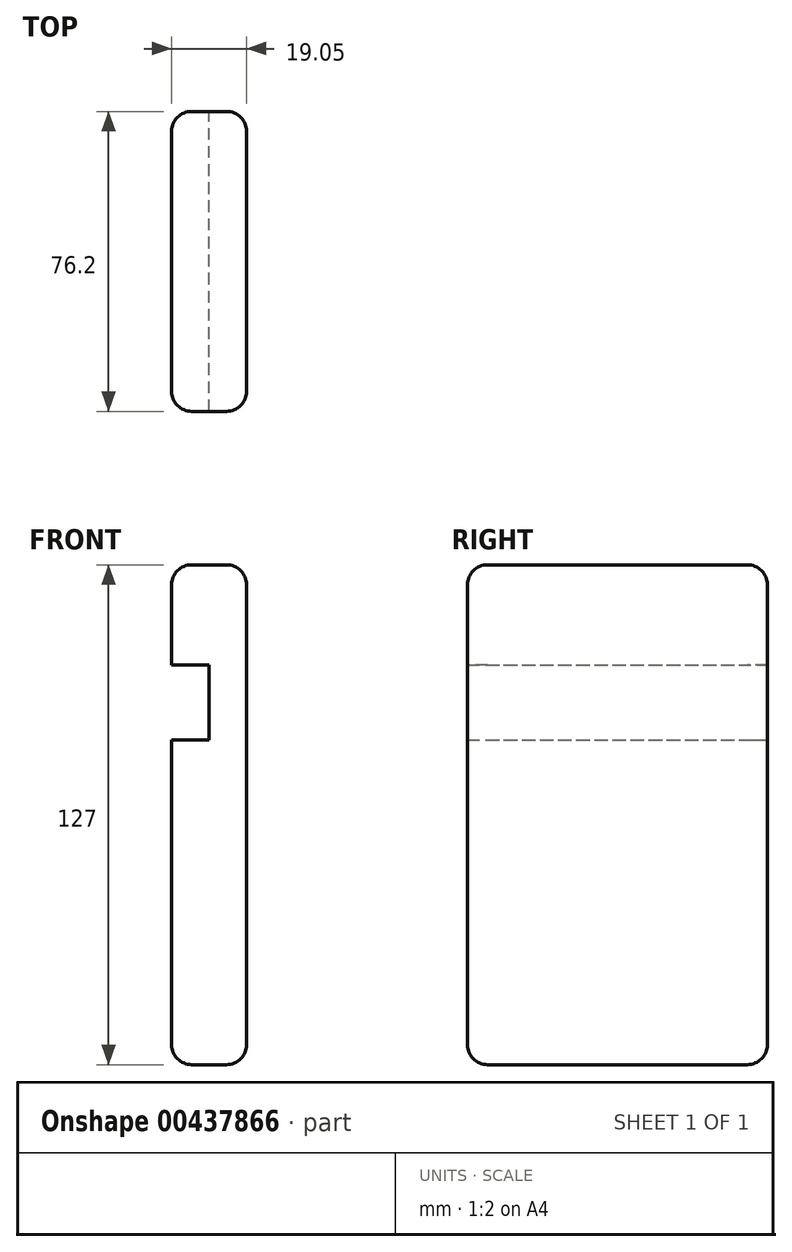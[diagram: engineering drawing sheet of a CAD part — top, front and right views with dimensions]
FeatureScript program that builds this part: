
annotation { "Feature Type Name" : "Feature", "Feature Type Description" : "" }
export const myFeature = defineFeature(function(context is Context, id is Id, definition is map)
    precondition{}
    {
        {
            var Q0;
            Q0=qCreatedBy(makeId("Front.planeOp"),FACE);
            var sketch = newSketch(context, id + "F0", { "sketchPlane" : qUnion([Q0])});
            skLineSegment(sketch, "E0", {"start": v(27.83, 69.22) * mm, "end": v(27.83, -57.78) * mm});
            skLineSegment(sketch, "E1", {"start": v(27.83, -57.78) * mm, "end": v(8.78, -57.78) * mm});
            skLineSegment(sketch, "E2", {"start": v(27.83, 69.22) * mm, "end": v(8.78, 69.22) * mm});
            skLineSegment(sketch, "E3", {"start": v(8.78, 69.22) * mm, "end": v(8.78, 43.82) * mm});
            skLineSegment(sketch, "E4", {"start": v(8.78, 43.82) * mm, "end": v(18.3, 43.82) * mm});
            skLineSegment(sketch, "E5", {"start": v(18.3, 43.82) * mm, "end": v(18.3, 24.77) * mm});
            skLineSegment(sketch, "E6", {"start": v(18.3, 24.77) * mm, "end": v(8.78, 24.77) * mm});
            skLineSegment(sketch, "E7", {"start": v(8.78, 24.77) * mm, "end": v(8.78, -57.78) * mm});
            skSolve(sketch);
        }
        {
            var Q0;
            Q0 = qSketchRegion(id + "F0", true);
            extrude(context, id + "F1", {"entities" : qUnion([Q0]), "depth" : 76.2 * mm});
        }
        {
            var Q0;
            Q0=makeQuery(id+"F1.opExtrude","CAP_EDGE",EDGE,{"disambiguationData":[OSD([sQuery(id+"F0.wireOp",EDGE,"E2")])],"isStart":false});
            var Q1;
            Q1=makeQuery(id+"F1.opExtrude","CAP_EDGE",EDGE,{"disambiguationData":[OSD([sQuery(id+"F0.wireOp",EDGE,"E3")])],"isStart":false});
            var Q2;
            Q2=makeQuery(id+"F1.opExtrude","CAP_EDGE",EDGE,{"disambiguationData":[OSD([sQuery(id+"F0.wireOp",EDGE,"E0")])],"isStart":false});
            var Q3;
            Q3=makeQuery(id+"F1.opExtrude","CAP_EDGE",EDGE,{"disambiguationData":[OSD([sQuery(id+"F0.wireOp",EDGE,"E1")])],"isStart":false});
            var Q4;
            Q4=makeQuery(id+"F1.opExtrude","CAP_EDGE",EDGE,{"disambiguationData":[OSD([sQuery(id+"F0.wireOp",EDGE,"E7")])],"isStart":false});
            var Q5;
            Q5=makeQuery(id+"F1.opExtrude","SWEPT_EDGE",EDGE,{"disambiguationData":[OSD([sQuery(id+"F0.wireOp",EDGE,"E2"),sQuery(id+"F0.wireOp",EDGE,"E3")])]});
            var Q6;
            Q6=makeQuery(id+"F1.opExtrude","SWEPT_EDGE",EDGE,{"disambiguationData":[OSD([sQuery(id+"F0.wireOp",EDGE,"E1"),sQuery(id+"F0.wireOp",EDGE,"E7")])]});
            var Q7;
            Q7=makeQuery(id+"F1.opExtrude","CAP_EDGE",EDGE,{"disambiguationData":[OSD([sQuery(id+"F0.wireOp",EDGE,"E0")])],"isStart":true});
            var Q8;
            Q8=makeQuery(id+"F1.opExtrude","CAP_EDGE",EDGE,{"disambiguationData":[OSD([sQuery(id+"F0.wireOp",EDGE,"E2")])],"isStart":true});
            var Q9;
            Q9=makeQuery(id+"F1.opExtrude","CAP_EDGE",EDGE,{"disambiguationData":[OSD([sQuery(id+"F0.wireOp",EDGE,"E1")])],"isStart":true});
            var Q10;
            Q10=makeQuery(id+"F1.opExtrude","SWEPT_EDGE",EDGE,{"disambiguationData":[OSD([sQuery(id+"F0.wireOp",EDGE,"E0"),sQuery(id+"F0.wireOp",EDGE,"E2")])]});
            var Q11;
            Q11=makeQuery(id+"F1.opExtrude","SWEPT_EDGE",EDGE,{"disambiguationData":[OSD([sQuery(id+"F0.wireOp",EDGE,"E0"),sQuery(id+"F0.wireOp",EDGE,"E1")])]});
            var Q12;
            Q12=makeQuery(id+"F1.opExtrude","CAP_EDGE",EDGE,{"disambiguationData":[OSD([sQuery(id+"F0.wireOp",EDGE,"E3")])],"isStart":true});
            var Q13;
            Q13=makeQuery(id+"F1.opExtrude","CAP_EDGE",EDGE,{"disambiguationData":[OSD([sQuery(id+"F0.wireOp",EDGE,"E7")])],"isStart":true});
            fillet(context, id + "F2", {"entities" : qUnion([Q0, Q1, Q2, Q3, Q4, Q5, Q6, Q7, Q8, Q9, Q10, Q11, Q12, Q13]), "radius" : 5.08 * mm, "tangentPropagation" : true, "allowEdgeOverflow" : false});
        }
    });
